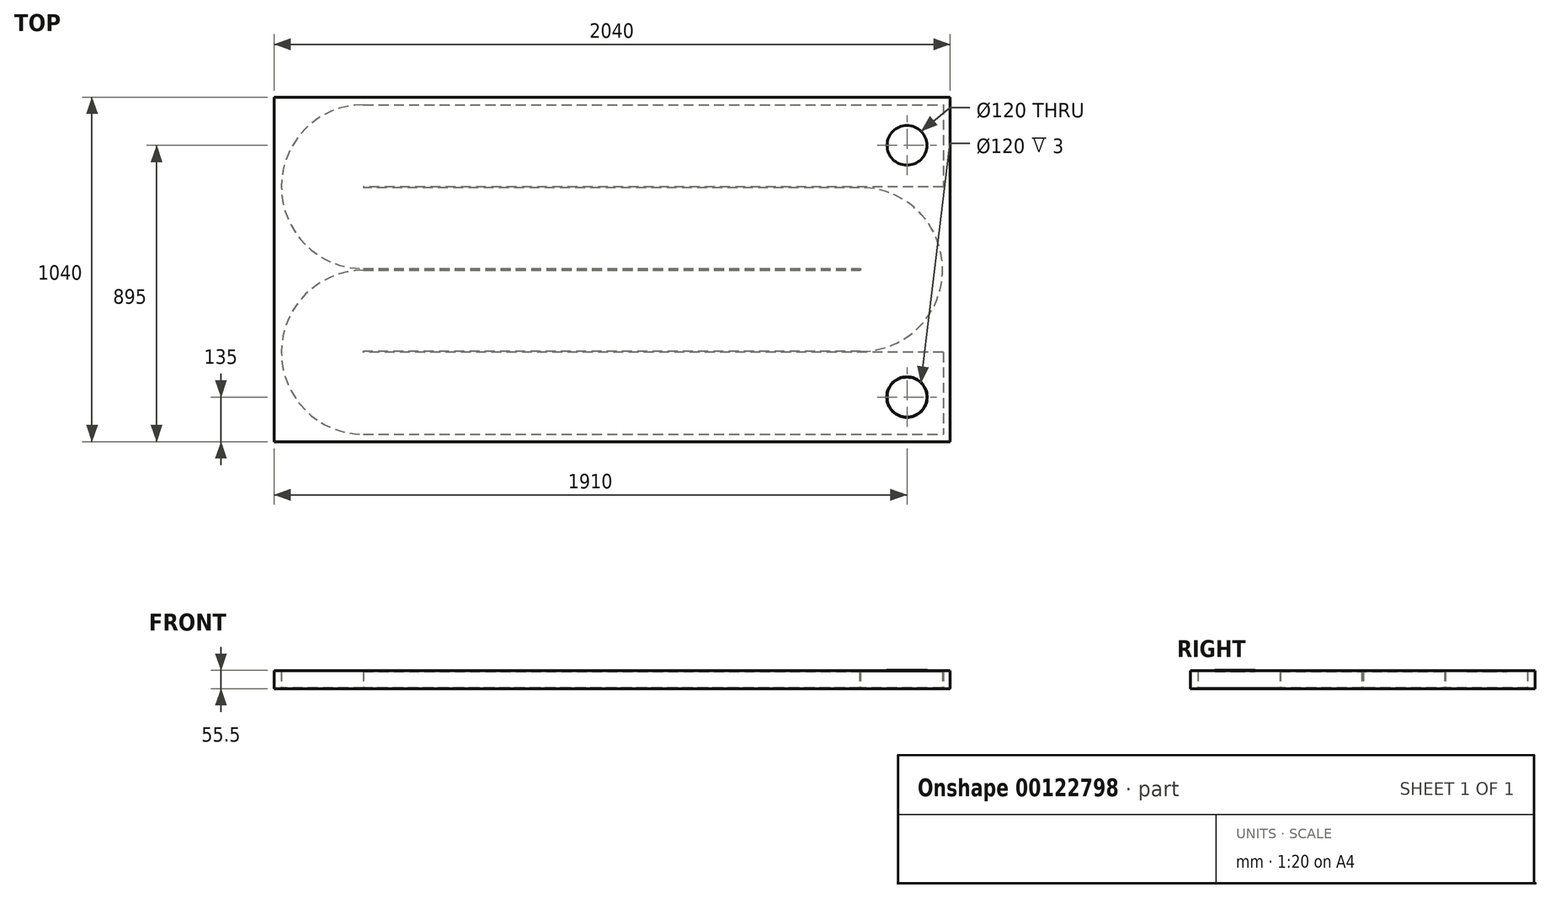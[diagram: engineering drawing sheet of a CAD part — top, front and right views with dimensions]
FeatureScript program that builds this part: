
annotation { "Feature Type Name" : "Feature", "Feature Type Description" : "" }
export const myFeature = defineFeature(function(context is Context, id is Id, definition is map)
    precondition{}
    {
        {
            var Q0;
            Q0=qCreatedBy(makeId("Top.planeOp"),FACE);
            var sketch = newSketch(context, id + "F0", { "sketchPlane" : qUnion([Q0])});
            skLineSegment(sketch, "E0.bottom", {"start": v(-1000, 500) * mm, "end": v(1000, 500) * mm});
            skLineSegment(sketch, "E0.top", {"start": v(-1000, -500) * mm, "end": v(1000, -500) * mm});
            skLineSegment(sketch, "E0.left", {"start": v(-1000, 500) * mm, "end": v(-1000, -500) * mm});
            skLineSegment(sketch, "E0.right", {"start": v(1000, 500) * mm, "end": v(1000, -500) * mm});
            skPoint(sketch, "E0.middle", {"position": v(0, 0) * mm});
            skLineSegment(sketch, "E1", {"start": v(1000, 250) * mm, "end": v(-750, 250) * mm});
            skLineSegment(sketch, "E2", {"start": v(-750, 0) * mm, "end": v(750, 0) * mm, "construction": true});
            skLineSegment(sketch, "E3", {"start": v(1000, -250) * mm, "end": v(-750, -250) * mm});
            skArc(sketch, "E4", {"start": v(-750, 500) * mm, "mid": v(-1000, 250) * mm, "end": v(-750, 0) * mm});
            skArc(sketch, "E5", {"start": v(-750, 0) * mm, "mid": v(-1000, -250) * mm, "end": v(-750, -500) * mm});
            skLineSegment(sketch, "E6.0", {"start": v(746.85, 247.48) * mm, "end": v(-750, 247.48) * mm});
            skLineSegment(sketch, "E7.0", {"start": v(750, -247.5) * mm, "end": v(-750, -247.5) * mm});
            skLineSegment(sketch, "E8.0", {"start": v(-750, 2.5) * mm, "end": v(750, 2.5) * mm});
            skArc(sketch, "E9.0", {"start": v(-750, 497.5) * mm, "mid": v(-997.5, 250) * mm, "end": v(-750, 2.5) * mm});
            skLineSegment(sketch, "E10", {"start": v(-750, 497.5) * mm, "end": v(1000, 497.5) * mm});
            skLineSegment(sketch, "E11.0", {"start": v(-750, -2.5) * mm, "end": v(750, -2.5) * mm});
            skLineSegment(sketch, "E12", {"start": v(750, 2.5) * mm, "end": v(750, -2.5) * mm});
            skArc(sketch, "E13.1", {"start": v(-750, -2.5) * mm, "mid": v(-997.5, -250) * mm, "end": v(-750, -497.5) * mm});
            skLineSegment(sketch, "E14", {"start": v(-750, -497.5) * mm, "end": v(1000, -497.5) * mm});
            skLineSegment(sketch, "E15.bottom", {"start": v(-1020, 520) * mm, "end": v(1020, 520) * mm});
            skLineSegment(sketch, "E15.top", {"start": v(-1020, -520) * mm, "end": v(1020, -520) * mm});
            skLineSegment(sketch, "E15.left", {"start": v(-1020, 520) * mm, "end": v(-1020, -520) * mm});
            skLineSegment(sketch, "E15.right", {"start": v(1020, 520) * mm, "end": v(1020, -520) * mm});
            skArc(sketch, "E16", {"start": v(750, -250) * mm, "mid": v(1000, 0) * mm, "end": v(750, 250) * mm});
            skLineSegment(sketch, "E17", {"start": v(-750, -250) * mm, "end": v(-750, -247.5) * mm});
            skLineSegment(sketch, "E18", {"start": v(-750, 250) * mm, "end": v(-750, 247.48) * mm});
            skArc(sketch, "E19.0", {"start": v(750, -247.5) * mm, "mid": v(997.5, 1.57) * mm, "end": v(746.85, 247.48) * mm});
            skSolve(sketch);
        }
        {
            var Q0;
            Q0=makeQuery(id+"F0.imprint","IMPRINT",FACE,{"disambiguationData":[TD([[makeQuery(id+"F0.imprint","IMPRINT",EDGE,{"derivedFrom":sQuery(id+"F0.wireOp",EDGE,"E15.bottom")}),-1.0]])]});
            var Q1;
            {var subQ0=sQuery(id+"F0.wireOp",EDGE,"E0.left");var subQ1=sQuery(id+"F0.wireOp",EDGE,"E0.top");var subQ2=makeQuery(id+"F0.imprint","INTERSECT",VERTEX,{"derivedFrom":[subQ1,subQ0]});Q1=makeQuery(id+"F0.imprint","IMPRINT",FACE,{"disambiguationData":[TD([[makeQuery(id+"F0.imprint","IMPRINT",EDGE,{"disambiguationData":[TD([[subQ2,-1.0]])],"derivedFrom":subQ1}),1.0]])]});}
            var Q2;
            {var subQ0=sQuery(id+"F0.wireOp",EDGE,"E4");var subQ1=sQuery(id+"F0.wireOp",EDGE,"E0.left");var subQ2=makeQuery(id+"F0.imprint","INTERSECT",VERTEX,{"derivedFrom":[subQ1,subQ0]});Q2=makeQuery(id+"F0.imprint","IMPRINT",FACE,{"disambiguationData":[TD([[makeQuery(id+"F0.imprint","IMPRINT",EDGE,{"disambiguationData":[TD([[subQ2,-1.0]])],"derivedFrom":subQ1}),1.0]])]});}
            var Q3;
            {var subQ0=sQuery(id+"F0.wireOp",EDGE,"E0.left");var subQ1=sQuery(id+"F0.wireOp",EDGE,"E0.bottom");var subQ2=makeQuery(id+"F0.imprint","INTERSECT",VERTEX,{"derivedFrom":[subQ1,subQ0]});Q3=makeQuery(id+"F0.imprint","IMPRINT",FACE,{"disambiguationData":[TD([[makeQuery(id+"F0.imprint","IMPRINT",EDGE,{"disambiguationData":[TD([[subQ2,-1.0]])],"derivedFrom":subQ1}),-1.0]])]});}
            var Q4;
            {var subQ0=sQuery(id+"F0.wireOp",EDGE,"E1");var subQ1=sQuery(id+"F0.wireOp",EDGE,"E0.right");var subQ2=makeQuery(id+"F0.imprint","INTERSECT",VERTEX,{"derivedFrom":[subQ1,subQ0]});Q4=makeQuery(id+"F0.imprint","IMPRINT",FACE,{"disambiguationData":[TD([[makeQuery(id+"F0.imprint","IMPRINT",EDGE,{"disambiguationData":[TD([[subQ2,-1.0]])],"derivedFrom":subQ1}),-1.0]])]});}
            var Q5;
            {var subQ0=sQuery(id+"F0.wireOp",EDGE,"E3");var subQ1=sQuery(id+"F0.wireOp",EDGE,"E0.right");var subQ2=makeQuery(id+"F0.imprint","INTERSECT",VERTEX,{"derivedFrom":[subQ1,subQ0]});Q5=makeQuery(id+"F0.imprint","IMPRINT",FACE,{"disambiguationData":[TD([[makeQuery(id+"F0.imprint","IMPRINT",EDGE,{"disambiguationData":[TD([[subQ2,1.0]])],"derivedFrom":subQ1}),-1.0]])]});}
            var Q6;
            Q6=makeQuery(id+"F0.imprint","IMPRINT",FACE,{"disambiguationData":[TD([[makeQuery(id+"F0.imprint","IMPRINT",EDGE,{"derivedFrom":sQuery(id+"F0.wireOp",EDGE,"E6.0")}),-1.0]])]});
            var Q7;
            Q7=makeQuery(id+"F0.imprint","IMPRINT",FACE,{"disambiguationData":[TD([[makeQuery(id+"F0.imprint","IMPRINT",EDGE,{"derivedFrom":sQuery(id+"F0.wireOp",EDGE,"E8.0")}),-1.0]])]});
            extrude(context, id + "F1", {"entities" : qUnion([Q0, Q1, Q2, Q3, Q4, Q5, Q6, Q7]), "depth" : 50 * mm});
        }
        {
            var Q0;
            Q0=makeQuery(id+"F1.opExtrude","CAP_FACE",FACE,{"disambiguationData":[OSD([sQuery(id+"F0.wireOp",EDGE,"E0.right"),sQuery(id+"F0.wireOp",EDGE,"027c1220-4877-44cb-8764-8f065f8d1aa2.0"),sQuery(id+"F0.wireOp",EDGE,"E6.0"),sQuery(id+"F0.wireOp",EDGE,"KaQ5siDK-TaWD-7vQk-2lZJ-Glvynt1JZ8is"),sQuery(id+"F0.wireOp",EDGE,"E7.0"),sQuery(id+"F0.wireOp",EDGE,"fb1f04b5-cccc-48b9-9efb-247febb5027e.0"),sQuery(id+"F0.wireOp",EDGE,"1gYWqmdH-4qh5-cDue-I99Z-xdz35yHpbHhm"),sQuery(id+"F0.wireOp",EDGE,"E8.0"),sQuery(id+"F0.wireOp",EDGE,"E9.0"),sQuery(id+"F0.wireOp",EDGE,"E10"),sQuery(id+"F0.wireOp",EDGE,"E12"),sQuery(id+"F0.wireOp",EDGE,"E11.0"),sQuery(id+"F0.wireOp",EDGE,"E13.1"),sQuery(id+"F0.wireOp",EDGE,"E14"),sQuery(id+"F0.wireOp",EDGE,"E15.bottom"),sQuery(id+"F0.wireOp",EDGE,"E15.top"),sQuery(id+"F0.wireOp",EDGE,"E15.left"),sQuery(id+"F0.wireOp",EDGE,"E15.right")])],"isStart":false});
            var sketch = newSketch(context, id + "F2", { "sketchPlane" : qUnion([Q0])});
            skLineSegment(sketch, "E20.bottom", {"start": v(-1020, 520) * mm, "end": v(1020, 520) * mm});
            skLineSegment(sketch, "E20.top", {"start": v(-1020, -520) * mm, "end": v(1020, -520) * mm});
            skLineSegment(sketch, "E20.left", {"start": v(-1020, 520) * mm, "end": v(-1020, -520) * mm});
            skLineSegment(sketch, "E20.right", {"start": v(1020, 520) * mm, "end": v(1020, -520) * mm});
            skCircle(sketch, "E21", {"center": v(890, 375) * mm, "radius": 60 * mm});
            skCircle(sketch, "E22", {"center": v(890, -385) * mm, "radius": 60 * mm});
            skSolve(sketch);
        }
        {
            var Q0;
            Q0 = qSketchRegion(id + "F2", true);
            extrude(context, id + "F3", {"entities" : qUnion([Q0]), "operationType" : NewBodyOperationType.ADD, "depth" : 2.5 * mm});
        }
        {
            var Q0;
            Q0=makeQuery(id+"F1.opExtrude","CAP_FACE",FACE,{"disambiguationData":[OSD([sQuery(id+"F0.wireOp",EDGE,"E0.right"),sQuery(id+"F0.wireOp",EDGE,"027c1220-4877-44cb-8764-8f065f8d1aa2.0"),sQuery(id+"F0.wireOp",EDGE,"E6.0"),sQuery(id+"F0.wireOp",EDGE,"KaQ5siDK-TaWD-7vQk-2lZJ-Glvynt1JZ8is"),sQuery(id+"F0.wireOp",EDGE,"E7.0"),sQuery(id+"F0.wireOp",EDGE,"fb1f04b5-cccc-48b9-9efb-247febb5027e.0"),sQuery(id+"F0.wireOp",EDGE,"1gYWqmdH-4qh5-cDue-I99Z-xdz35yHpbHhm"),sQuery(id+"F0.wireOp",EDGE,"E8.0"),sQuery(id+"F0.wireOp",EDGE,"E9.0"),sQuery(id+"F0.wireOp",EDGE,"E10"),sQuery(id+"F0.wireOp",EDGE,"E12"),sQuery(id+"F0.wireOp",EDGE,"E11.0"),sQuery(id+"F0.wireOp",EDGE,"E13.1"),sQuery(id+"F0.wireOp",EDGE,"E14"),sQuery(id+"F0.wireOp",EDGE,"E15.bottom"),sQuery(id+"F0.wireOp",EDGE,"E15.top"),sQuery(id+"F0.wireOp",EDGE,"E15.left"),sQuery(id+"F0.wireOp",EDGE,"E15.right")])],"isStart":true});
            var sketch = newSketch(context, id + "F4", { "sketchPlane" : qUnion([Q0])});
            skLineSegment(sketch, "E23.bottom", {"start": v(-1020, -520) * mm, "end": v(1020, -520) * mm});
            skLineSegment(sketch, "E23.top", {"start": v(-1020, 520) * mm, "end": v(1020, 520) * mm});
            skLineSegment(sketch, "E23.left", {"start": v(-1020, -520) * mm, "end": v(-1020, 520) * mm});
            skLineSegment(sketch, "E23.right", {"start": v(1020, -520) * mm, "end": v(1020, 520) * mm});
            skSolve(sketch);
        }
        {
            var Q0;
            Q0 = qSketchRegion(id + "F4", true);
            extrude(context, id + "F5", {"entities" : qUnion([Q0]), "operationType" : NewBodyOperationType.ADD, "depth" : 2.5 * mm});
        }
        {
            var Q0;
            Q0=makeQuery(id+"F3.opExtrude","CAP_FACE",FACE,{"disambiguationData":[OSD([sQuery(id+"F2.wireOp",EDGE,"E20.bottom"),sQuery(id+"F2.wireOp",EDGE,"E20.top"),sQuery(id+"F2.wireOp",EDGE,"E20.left"),sQuery(id+"F2.wireOp",EDGE,"E20.right"),sQuery(id+"F2.wireOp",EDGE,"E21"),sQuery(id+"F2.wireOp",EDGE,"E22")])],"isStart":false});
            var sketch = newSketch(context, id + "F6", { "sketchPlane" : qUnion([Q0])});
            skCircle(sketch, "E24", {"center": v(890, -385) * mm, "radius": 61.25 * mm});
            skSolve(sketch);
        }
        {
            var Q0;
            Q0=makeQuery(id+"F6.imprint","IMPRINT",FACE,{"disambiguationData":[TD([[makeQuery(id+"F6.imprint","IMPRINT",EDGE,{"derivedFrom":sQuery(id+"F6.wireOp",EDGE,"E24")}),1.0]])]});
            extrude(context, id + "F7", {"entities" : qUnion([Q0]), "operationType" : NewBodyOperationType.ADD, "depth" : 0.5 * mm});
        }
    });
